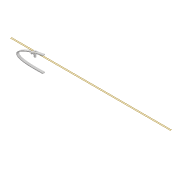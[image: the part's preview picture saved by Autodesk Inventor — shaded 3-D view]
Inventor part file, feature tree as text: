
AUTODESK INVENTOR PART (.ipt)
format: ipt  version: 2022 (Build 260153000, 153)  size: 648,704 bytes
history: native  units: mm
features: extrude x13, sketch x11, projected_geometry x9, plane x4, shell x1, fillet x1
ambient origin geometry x8: Origin, YZ Plane, XZ Plane, XY Plane, X Axis, Y Axis, Z Axis, Center Point
bodies: Solid1 (feature_tree)
feature tree (39):
  extrude  "Extrusion1"  Depth=3.0mm
  shell  "Shell1"  Thickness=5.215mm
  plane  "Work Plane3"
  sketch  "Sketch26"  dims[d69=4.1mm d70=63.6mm]
  plane  "Work Plane4"
  extrude  "Extrusion9"  Depth=63.6mm
  plane  "Work Plane5"
  sketch  "Sketch38"  dims[d88=2.0mm d89=4.0mm]
  extrude  "Extrusion10"  Depth=4.2mm
  extrude  "Extrusion11"  Depth=6.0mm
  extrude  "Extrusion12"  Depth=21.0mm TaperAngle=0.0deg
  plane  "Work Plane6"
  extrude  "Extrusion13"  Depth=5.0mm
  extrude  "Extrusion15"  Depth=3.0mm TaperAngle=0.0deg
  extrude  "Extrusion16"  Depth=2.0mm
  extrude  "Extrusion17"  Depth=4.0mm
  extrude  "Extrusion20"  Depth=3.0mm TaperAngle=0.0deg
  fillet  "Fillet2"  Radius=12.0mm
  extrude  "Extrusion18"  Depth=28.0mm
  extrude  "Extrusion21"  Depth=9.0mm TaperAngle=0.0deg
  extrude  "Extrusion22"  Depth=200.0mm
  sketch  "Sketch3"  dims[d0=12.0mm d1=0.0mm d2=3.0mm d68=5.215mm]
  sketch  "Sketch27"  dims[d71=16.0mm d72=4.2mm]
  projected_geometry  "Projected Loop13"
  sketch  "Sketch29"  dims[d73=63.6mm d74=6.0mm]
  sketch  "Sketch30"  dims[d75=7.0mm d76=21.0mm d77=0.0mm]
  projected_geometry  "Projected Loop14"
  sketch  "Sketch31"  dims[d78=-11.0mm d79=5.0mm]
  projected_geometry  "Projected Loop15"
  projected_geometry  "Projected Loop16"
  projected_geometry  "Projected Loop17"
  sketch  "Sketch33"  dims[d80=10.0mm d83=3.0mm d84=0.0mm]
  projected_geometry  "Projected Loop18"
  projected_geometry  "Projected Loop19"
  sketch  "Sketch36"  dims[d86=0.65mm d87=2.0mm]
  projected_geometry  "Projected Loop20"
  sketch  "Sketch39"  dims[d90=4.0mm d91=3.0mm d92=0.0mm d93=12.0mm]
  sketch  "Sketch41"  dims[d94=6.5mm d95=0.0mm d96=28.0mm d98=9.0mm d99=0.0mm d103=200.0mm d104=100.0mm d105=0.0mm d106=7.0mm d107=4.1mm d108=7.0mm d109=2.0mm d110=0.0mm d111=2.0mm d112=0.0mm d113=2.0mm d114=95.0mm d115=10.0mm d116=0.0mm d119=100.0mm d120=0.0mm d121=1.0mm d122=3.0mm d123=0.0mm d124=10.0mm d125=0.0mm]
  projected_geometry  "Project Cut Edges1"
